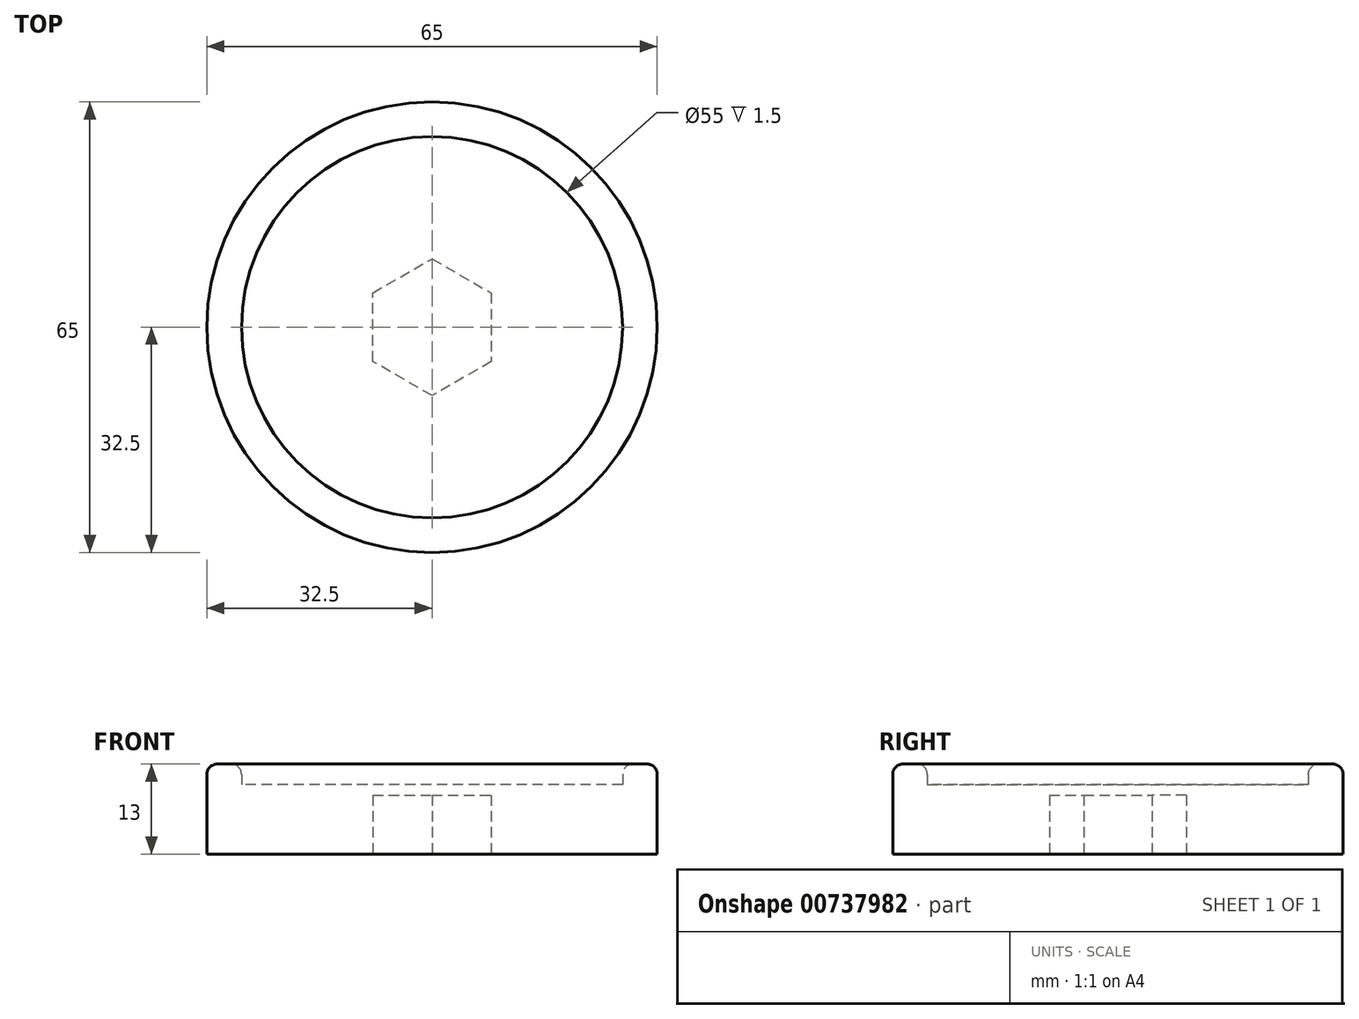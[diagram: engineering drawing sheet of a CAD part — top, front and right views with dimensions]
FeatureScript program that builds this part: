
annotation { "Feature Type Name" : "Feature", "Feature Type Description" : "" }
export const myFeature = defineFeature(function(context is Context, id is Id, definition is map)
    precondition{}
    {
        {
            var Q0;
            Q0=qCreatedBy(makeId("Top.planeOp"),FACE);
            var sketch = newSketch(context, id + "F0", { "sketchPlane" : qUnion([Q0])});
            skCircle(sketch, "E0", {"center": v(0, 0) * mm, "radius": 32.5 * mm});
            skCircle(sketch, "E1.cCircle", {"center": v(0, 0) * mm, "radius": 9.87 * mm, "construction": true});
            skLineSegment(sketch, "E1.0", {"start": v(0, 9.87) * mm, "end": v(8.55, 4.94) * mm});
            skLineSegment(sketch, "E1.1", {"start": v(8.55, 4.94) * mm, "end": v(8.55, -4.94) * mm});
            skLineSegment(sketch, "E1.2", {"start": v(8.55, -4.94) * mm, "end": v(0, -9.87) * mm});
            skLineSegment(sketch, "E1.3", {"start": v(0, -9.87) * mm, "end": v(-8.55, -4.94) * mm});
            skLineSegment(sketch, "E1.4", {"start": v(-8.55, -4.94) * mm, "end": v(-8.55, 4.94) * mm});
            skLineSegment(sketch, "E1.5", {"start": v(-8.55, 4.94) * mm, "end": v(0, 9.87) * mm});
            skCircle(sketch, "E2.0", {"center": v(0, 0) * mm, "radius": 27.5 * mm});
            skSolve(sketch);
        }
        {
            var Q0;
            Q0 = qSketchRegion(id + "F0", true);
            var Q1;
            Q1=makeQuery(id+"F0.imprint","IMPRINT",FACE,{"disambiguationData":[TD([[makeQuery(id+"F0.imprint","IMPRINT",EDGE,{"derivedFrom":sQuery(id+"F0.wireOp",EDGE,"E1.0")}),-1.0]])]});
            var Q2;
            Q2=makeQuery(id+"F0.imprint","IMPRINT",FACE,{"disambiguationData":[TD([[makeQuery(id+"F0.imprint","IMPRINT",EDGE,{"derivedFrom":sQuery(id+"F0.wireOp",EDGE,"E1.0")}),1.0]])]});
            extrude(context, id + "F1", {"entities" : qUnion([Q0, Q1, Q2]), "depth" : 10 * mm, "offsetDistance" : 25 * mm});
        }
        {
            var Q0;
            Q0=makeQuery(id+"F0.imprint","IMPRINT",FACE,{"disambiguationData":[TD([[makeQuery(id+"F0.imprint","IMPRINT",EDGE,{"derivedFrom":sQuery(id+"F0.wireOp",EDGE,"E1.0")}),-1.0]])]});
            extrude(context, id + "F2", {"entities" : qUnion([Q0]), "operationType" : NewBodyOperationType.REMOVE, "depth" : 8.5 * mm, "offsetDistance" : 25 * mm});
        }
        {
            var Q0;
            Q0=makeQuery(id+"F0.imprint","IMPRINT",FACE,{"disambiguationData":[TD([[makeQuery(id+"F0.imprint","IMPRINT",EDGE,{"derivedFrom":sQuery(id+"F0.wireOp",EDGE,"E0")}),1.0]])]});
            extrude(context, id + "F3", {"entities" : qUnion([Q0]), "operationType" : NewBodyOperationType.ADD, "depth" : 13 * mm, "offsetDistance" : 25 * mm});
        }
        {
            var Q0;
            Q0=makeQuery(id+"F3.opExtrude","CAP_EDGE",EDGE,{"disambiguationData":[OSD([sQuery(id+"F0.wireOp",EDGE,"E0")])],"isStart":false});
            var Q1;
            Q1=makeQuery(id+"F3.opExtrude","CAP_EDGE",EDGE,{"disambiguationData":[OSD([sQuery(id+"F0.wireOp",EDGE,"E2.0")])],"isStart":false});
            fillet(context, id + "F4", {"entities" : qUnion([Q0, Q1]), "radius" : 1.5 * mm, "tangentPropagation" : true, "allowEdgeOverflow" : false});
        }
    });
